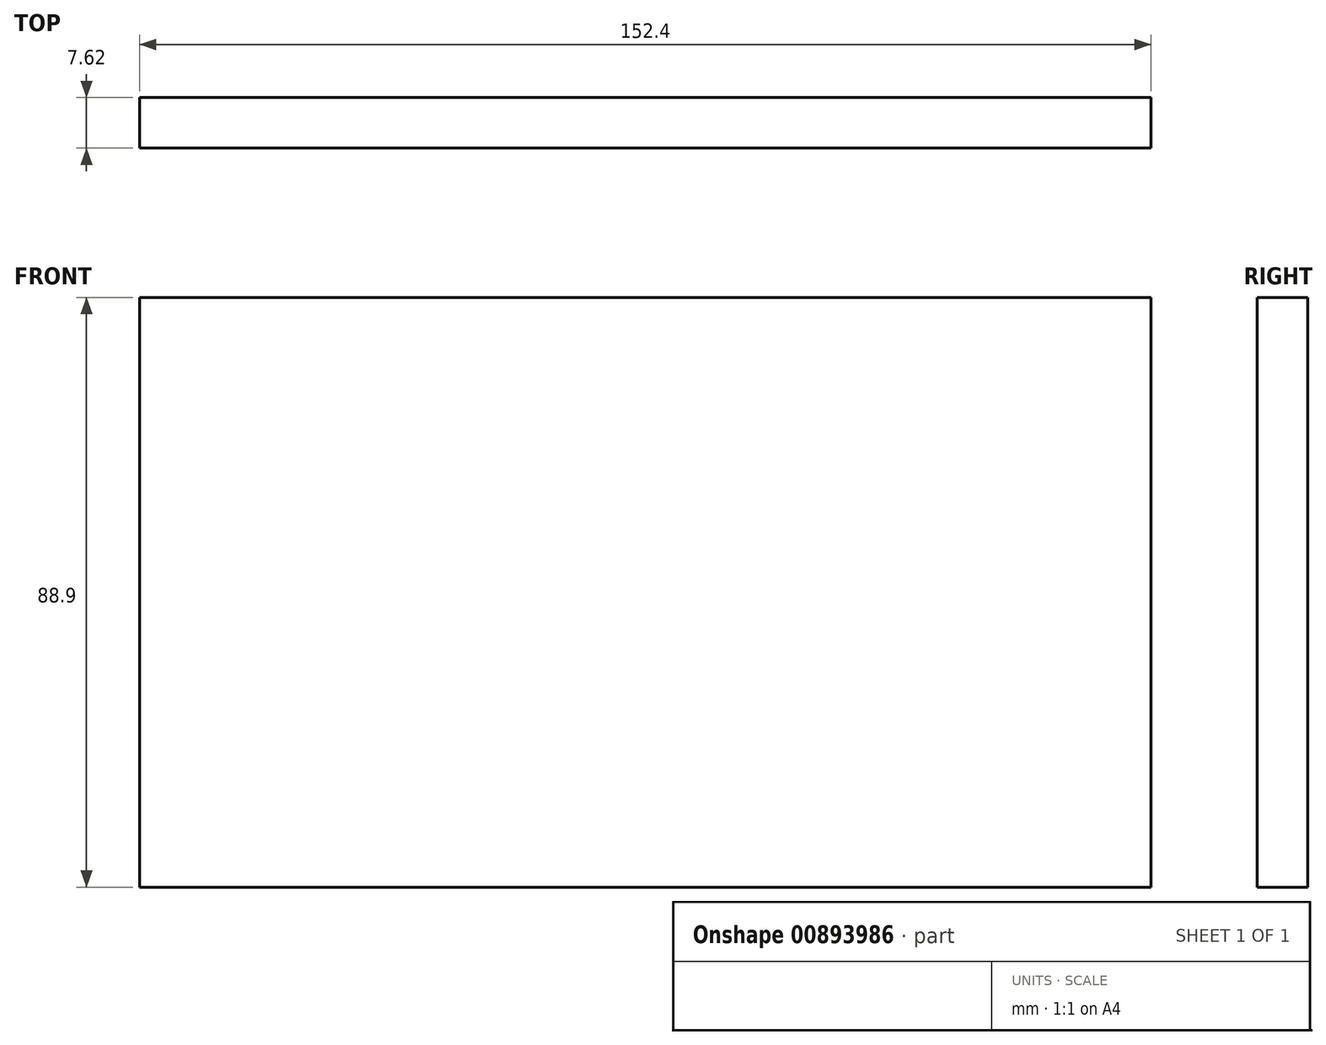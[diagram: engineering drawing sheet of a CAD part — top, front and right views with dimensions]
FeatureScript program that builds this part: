
annotation { "Feature Type Name" : "Feature", "Feature Type Description" : "" }
export const myFeature = defineFeature(function(context is Context, id is Id, definition is map)
    precondition{}
    {
        {
            var Q0;
            Q0=qCreatedBy(makeId("Front.planeOp"),FACE);
            var sketch = newSketch(context, id + "F0", { "sketchPlane" : qUnion([Q0])});
            skLineSegment(sketch, "E0.bottom", {"start": v(-152.4, 44.45) * mm, "end": v(0, 44.45) * mm});
            skLineSegment(sketch, "E0.top", {"start": v(-152.4, -44.45) * mm, "end": v(0, -44.45) * mm});
            skLineSegment(sketch, "E0.left", {"start": v(-152.4, 44.45) * mm, "end": v(-152.4, -44.45) * mm});
            skLineSegment(sketch, "E0.right", {"start": v(0, 44.45) * mm, "end": v(0, -44.45) * mm});
            skSolve(sketch);
        }
        {
            var Q0;
            Q0 = qSketchRegion(id + "F0", true);
            extrude(context, id + "F1", {"entities" : qUnion([Q0]), "depth" : 7.62 * mm, "offsetDistance" : 25.4 * mm});
        }
    });
